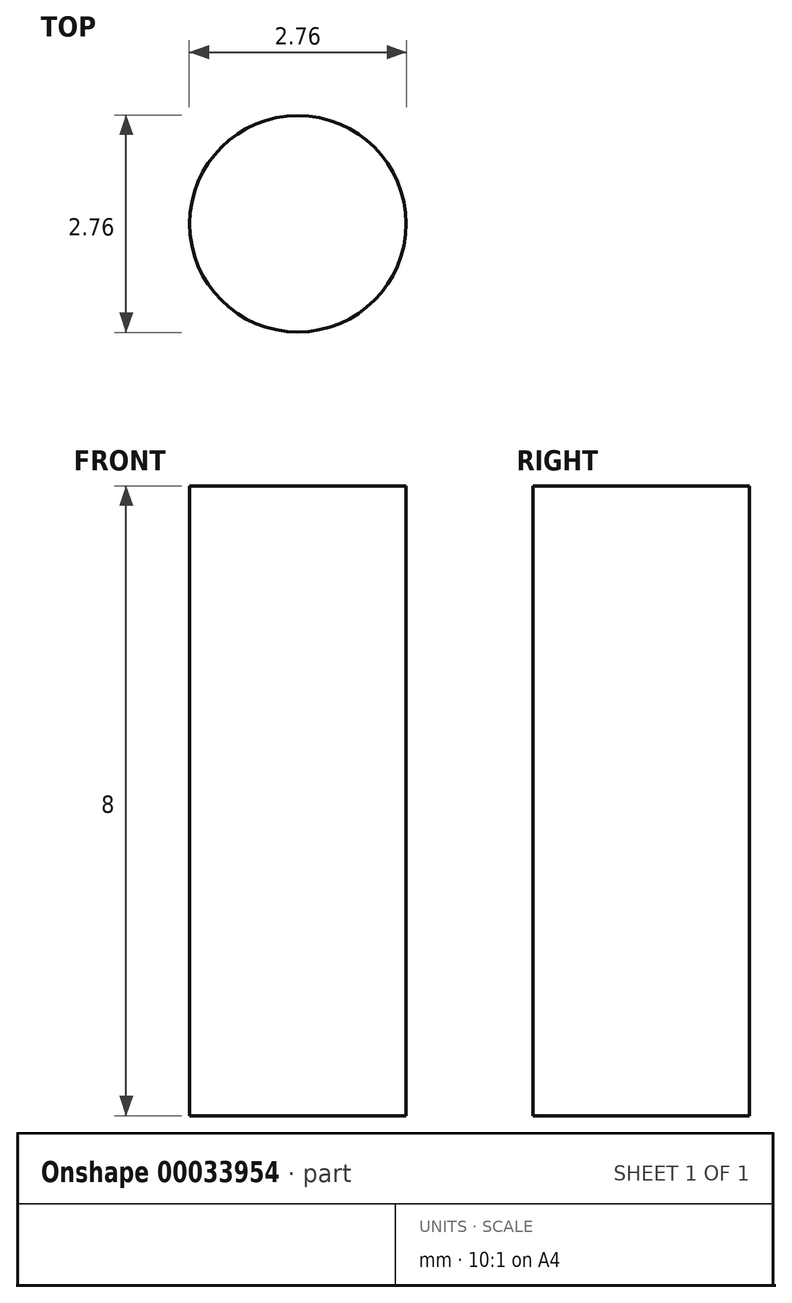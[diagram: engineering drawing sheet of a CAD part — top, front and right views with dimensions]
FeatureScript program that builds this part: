
annotation { "Feature Type Name" : "Feature", "Feature Type Description" : "" }
export const myFeature = defineFeature(function(context is Context, id is Id, definition is map)
    precondition{}
    {
        {
            var Q0;
            Q0=qCreatedBy(makeId("Top.planeOp"),FACE);
            var sketch = newSketch(context, id + "F0", { "sketchPlane" : qUnion([Q0])});
            skCircle(sketch, "E0", {"center": v(0, 0) * mm, "radius": 1.38 * mm});
            skSolve(sketch);
        }
        {
            var Q0;
            Q0=qSketchRegion(id+"F0",true);
            extrude(context, id + "F1", {"entities" : qUnion([Q0]), "depth" : 8 * mm});
        }
    });
